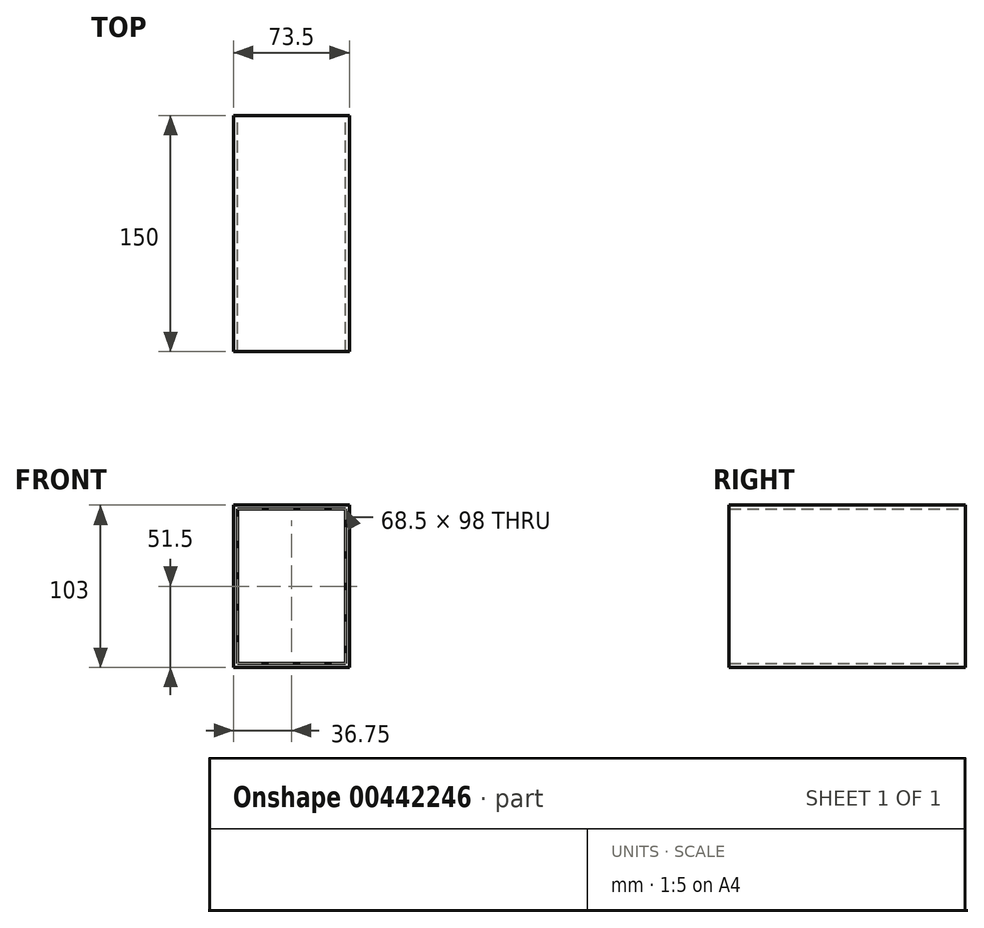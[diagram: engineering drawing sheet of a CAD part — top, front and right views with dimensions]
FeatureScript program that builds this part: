
annotation { "Feature Type Name" : "Feature", "Feature Type Description" : "" }
export const myFeature = defineFeature(function(context is Context, id is Id, definition is map)
    precondition{}
    {
        {
            var Q0;
            Q0=qCreatedBy(makeId("Front.planeOp"),FACE);
            var sketch = newSketch(context, id + "F0", { "sketchPlane" : qUnion([Q0])});
            skLineSegment(sketch, "E0.bottom", {"start": v(-36.75, 51.5) * mm, "end": v(36.75, 51.5) * mm});
            skLineSegment(sketch, "E0.top", {"start": v(-36.75, -51.5) * mm, "end": v(36.75, -51.5) * mm});
            skLineSegment(sketch, "E0.left", {"start": v(-36.75, 51.5) * mm, "end": v(-36.75, -51.5) * mm});
            skLineSegment(sketch, "E0.right", {"start": v(36.75, 51.5) * mm, "end": v(36.75, -51.5) * mm});
            skPoint(sketch, "E0.middle", {"position": v(0, 0) * mm});
            skLineSegment(sketch, "E1.0", {"start": v(-34.25, 49) * mm, "end": v(34.25, 49) * mm});
            skLineSegment(sketch, "E1.1", {"start": v(-34.25, 49) * mm, "end": v(-34.25, -49) * mm});
            skLineSegment(sketch, "E1.2", {"start": v(-34.25, -49) * mm, "end": v(34.25, -49) * mm});
            skLineSegment(sketch, "E1.3", {"start": v(34.25, 49) * mm, "end": v(34.25, -49) * mm});
            skSolve(sketch);
        }
        {
            var Q0;
            Q0=makeQuery(id+"F0.imprint","IMPRINT",FACE,{"disambiguationData":[TD([[makeQuery(id+"F0.imprint","IMPRINT",EDGE,{"derivedFrom":sQuery(id+"F0.wireOp",EDGE,"E0.bottom")}),-1.0]])]});
            extrude(context, id + "F1", {"entities" : qUnion([Q0]), "depth" : 150 * mm});
        }
    });
